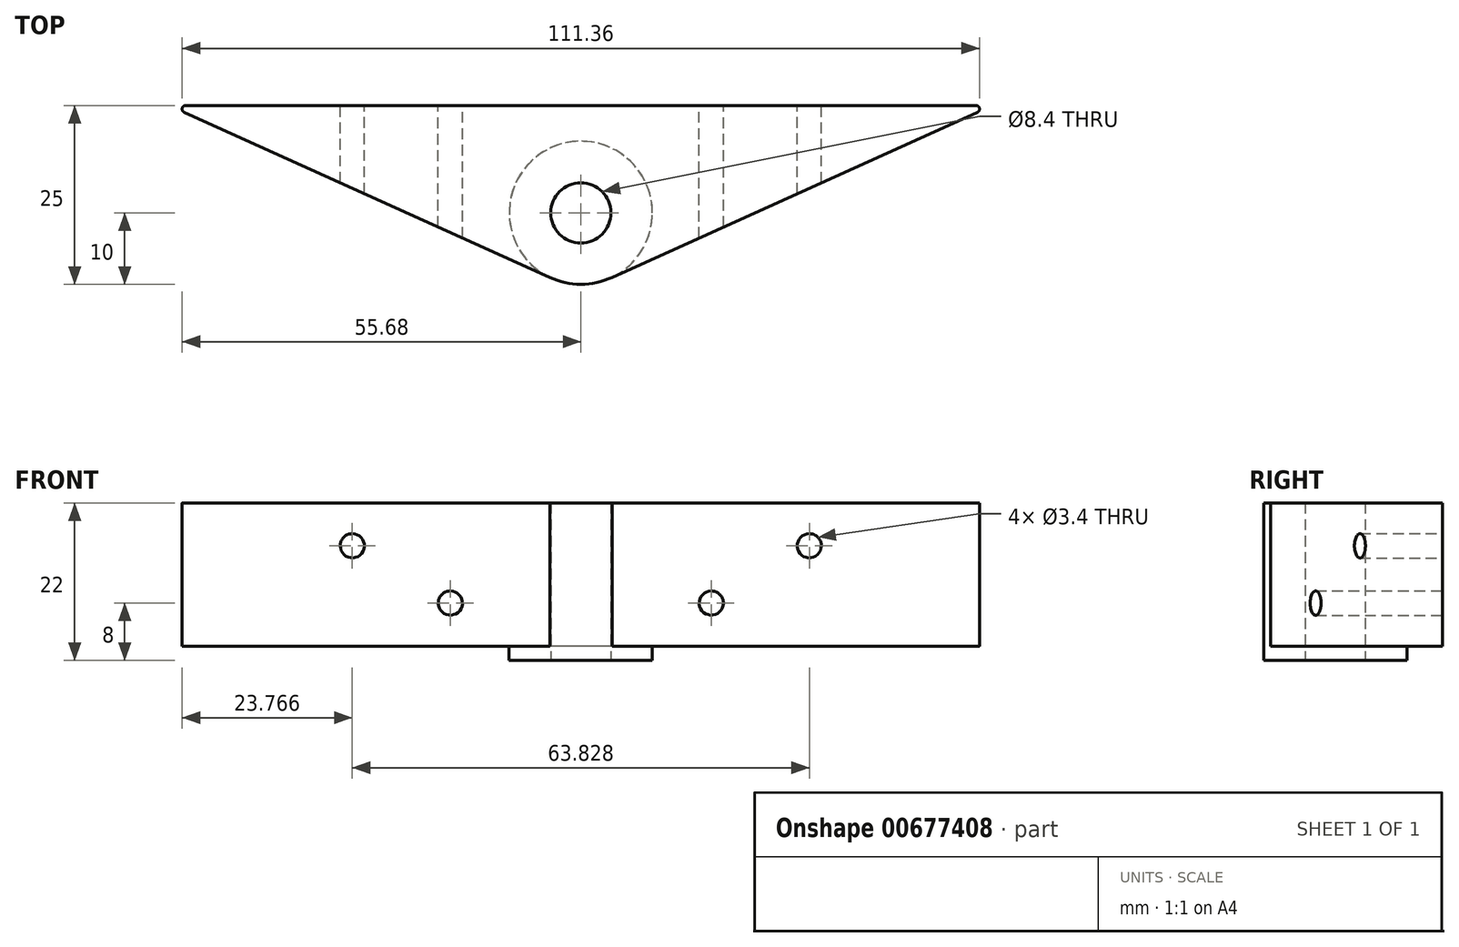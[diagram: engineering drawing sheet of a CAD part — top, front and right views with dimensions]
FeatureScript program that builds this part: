
annotation { "Feature Type Name" : "Feature", "Feature Type Description" : "" }
export const myFeature = defineFeature(function(context is Context, id is Id, definition is map)
    precondition{}
    {
        {
            var Q0;
            Q0=qCreatedBy(makeId("Top.planeOp"),FACE);
            var sketch = newSketch(context, id + "F0", { "sketchPlane" : qUnion([Q0])});
            skArc(sketch, "E0", {"start": v(-4.35, -24) * mm, "mid": v(0, -25) * mm, "end": v(4.35, -24) * mm});
            skCircle(sketch, "E1", {"center": v(0, -15) * mm, "radius": 4.2 * mm});
            skLineSegment(sketch, "E2.top", {"start": v(55.18, 0) * mm, "end": v(-55.18, 0) * mm});
            skLineSegment(sketch, "E2.left", {"start": v(57.5, 0) * mm, "end": v(57.5, 0) * mm});
            skLineSegment(sketch, "E2.right", {"start": v(-57.5, 0) * mm, "end": v(-57.5, 0) * mm});
            skLineSegment(sketch, "E3", {"start": v(55.38, -0.96) * mm, "end": v(4.35, -24) * mm});
            skLineSegment(sketch, "E4", {"start": v(-4.35, -24) * mm, "end": v(-55.38, -0.96) * mm});
            skPoint(sketch, "E5.visualSharp", {"position": v(-57.5, 0) * mm});
            skArc(sketch, "E5.filletArc", {"start": v(-55.18, 0) * mm, "mid": v(-55.67, -0.4) * mm, "end": v(-55.38, -0.96) * mm});
            skPoint(sketch, "E6.visualSharp", {"position": v(57.5, 0) * mm});
            skArc(sketch, "E6.filletArc", {"start": v(55.38, -0.96) * mm, "mid": v(55.67, -0.4) * mm, "end": v(55.18, 0) * mm});
            skSolve(sketch);
        }
        {
            var Q0;
            {var subQ1=sQuery(id+"F0.wireOp",EDGE,"E0");Q0=makeQuery(id+"F0.imprint","IMPRINT",FACE,{"disambiguationData":[TD([[makeQuery(id+"F0.imprint","IMPRINT",EDGE,{"derivedFrom":subQ1}),1.0]])]});}
            extrude(context, id + "F1", {"entities" : qUnion([Q0]), "depth" : 20 * mm, "offsetDistance" : 25 * mm});
        }
        {
            var Q0;
            Q0=makeQuery(id+"F1.opExtrude","CAP_FACE",FACE,{"disambiguationData":[OSD([sQuery(id+"F0.wireOp",EDGE,"E0"),sQuery(id+"F0.wireOp",EDGE,"E1"),sQuery(id+"F0.wireOp",EDGE,"E2.top"),sQuery(id+"F0.wireOp",EDGE,"E3"),sQuery(id+"F0.wireOp",EDGE,"E4"),sQuery(id+"F0.wireOp",EDGE,"E5.filletArc"),sQuery(id+"F0.wireOp",EDGE,"E6.filletArc")])],"isStart":true});
            var sketch = newSketch(context, id + "F2", { "sketchPlane" : qUnion([Q0])});
            skCircle(sketch, "E7", {"center": v(0, 15) * mm, "radius": 10 * mm});
            skCircle(sketch, "E8.0", {"center": v(0, 15) * mm, "radius": 4.2 * mm});
            skSolve(sketch);
        }
        {
            var Q0;
            Q0 = qSketchRegion(id + "F2", true);
            extrude(context, id + "F3", {"entities" : qUnion([Q0]), "operationType" : NewBodyOperationType.ADD, "depth" : 2 * mm, "offsetDistance" : 25 * mm});
        }
        {
            var Q0;
            Q0=makeQuery(id+"F1.opExtrude","SWEPT_FACE",FACE,{"disambiguationData":[OSD([sQuery(id+"F0.wireOp",EDGE,"E2.top")])]});
            var sketch = newSketch(context, id + "F4", { "sketchPlane" : qUnion([Q0])});
            skCircle(sketch, "E9", {"center": v(18.21, 6) * mm, "radius": 1.7 * mm});
            skCircle(sketch, "E10", {"center": v(-18.21, 6) * mm, "radius": 1.7 * mm});
            skCircle(sketch, "E11", {"center": v(31.91, 14) * mm, "radius": 1.7 * mm});
            skCircle(sketch, "E12", {"center": v(-31.91, 14) * mm, "radius": 1.7 * mm});
            skSolve(sketch);
        }
        {
            var Q0;
            Q0=makeQuery(id+"F4.imprint","IMPRINT",FACE,{"disambiguationData":[TD([[makeQuery(id+"F4.imprint","IMPRINT",EDGE,{"derivedFrom":sQuery(id+"F4.wireOp",EDGE,"E12")}),1.0]])]});
            var Q1;
            Q1=makeQuery(id+"F4.imprint","IMPRINT",FACE,{"disambiguationData":[TD([[makeQuery(id+"F4.imprint","IMPRINT",EDGE,{"derivedFrom":sQuery(id+"F4.wireOp",EDGE,"E10")}),1.0]])]});
            var Q2;
            Q2=makeQuery(id+"F4.imprint","IMPRINT",FACE,{"disambiguationData":[TD([[makeQuery(id+"F4.imprint","IMPRINT",EDGE,{"derivedFrom":sQuery(id+"F4.wireOp",EDGE,"E9")}),1.0]])]});
            var Q3;
            Q3=makeQuery(id+"F4.imprint","IMPRINT",FACE,{"disambiguationData":[TD([[makeQuery(id+"F4.imprint","IMPRINT",EDGE,{"derivedFrom":sQuery(id+"F4.wireOp",EDGE,"E11")}),1.0]])]});
            extrude(context, id + "F5", {"entities" : qUnion([Q0, Q1, Q2, Q3]), "operationType" : NewBodyOperationType.REMOVE, "oppositeDirection" : true, "depth" : 25 * mm, "offsetDistance" : 25 * mm});
        }
    });
